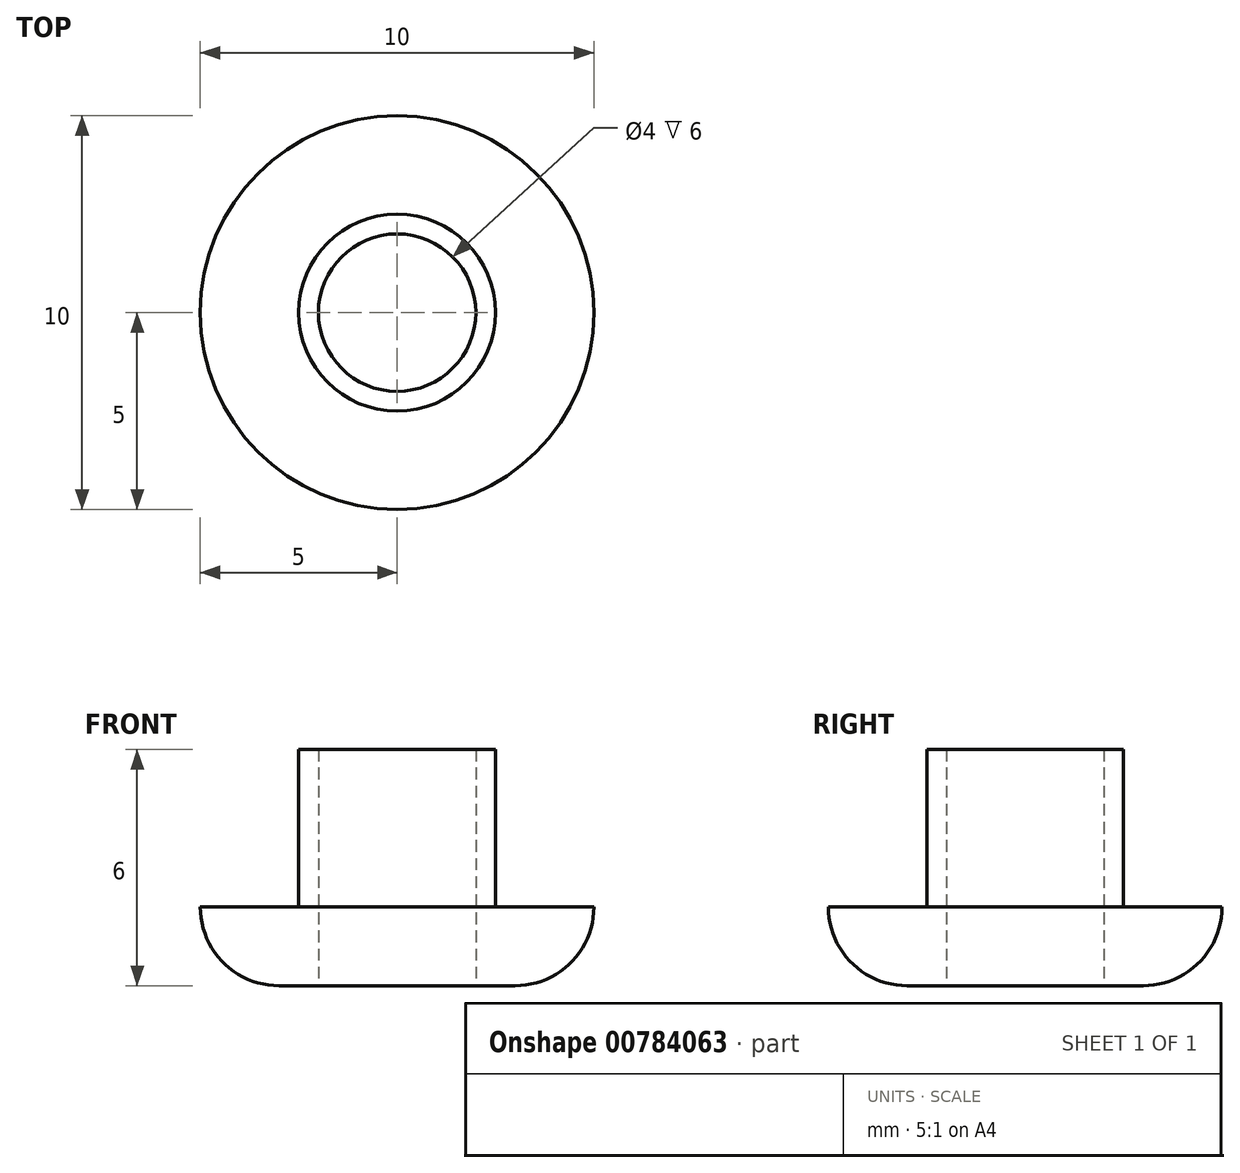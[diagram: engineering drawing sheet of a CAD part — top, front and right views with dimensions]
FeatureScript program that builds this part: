
annotation { "Feature Type Name" : "Feature", "Feature Type Description" : "" }
export const myFeature = defineFeature(function(context is Context, id is Id, definition is map)
    precondition{}
    {
        {
            var Q0;
            Q0=qCreatedBy(makeId("Top.planeOp"),FACE);
            var sketch = newSketch(context, id + "F0", { "sketchPlane" : qUnion([Q0])});
            skCircle(sketch, "E0", {"center": v(0, 0) * mm, "radius": 5 * mm});
            skCircle(sketch, "E1", {"center": v(0, 0) * mm, "radius": 2 * mm});
            skSolve(sketch);
        }
        {
            var Q0;
            Q0=makeQuery(id+"F0.imprint","IMPRINT",FACE,{"disambiguationData":[TD([[makeQuery(id+"F0.imprint","IMPRINT",EDGE,{"derivedFrom":sQuery(id+"F0.wireOp",EDGE,"E0")}),1.0]])]});
            var sketch = newSketch(context, id + "F1", { "sketchPlane" : qUnion([Q0])});
            skSolve(sketch);
        }
        {
            var Q0;
            Q0 = qSketchRegion(id + "F1", true);
            var Q1;
            Q1=makeQuery(id+"F0.imprint","IMPRINT",FACE,{"disambiguationData":[TD([[makeQuery(id+"F0.imprint","IMPRINT",EDGE,{"derivedFrom":sQuery(id+"F0.wireOp",EDGE,"E0")}),1.0]])]});
            extrude(context, id + "F2", {"entities" : qUnion([Q0, Q1]), "depth" : 2 * mm, "offsetDistance" : 25 * mm});
        }
        {
            var Q0;
            Q0=makeQuery(id+"F2.opExtrude","CAP_FACE",FACE,{"disambiguationData":[OSD([sQuery(id+"F0.wireOp",EDGE,"E0"),sQuery(id+"F0.wireOp",EDGE,"E1")])],"isStart":false});
            var sketch = newSketch(context, id + "F3", { "sketchPlane" : qUnion([Q0])});
            skCircle(sketch, "E2", {"center": v(0, 0) * mm, "radius": 2 * mm});
            skCircle(sketch, "E3", {"center": v(0, 0) * mm, "radius": 2.5 * mm});
            skSolve(sketch);
        }
        {
            var Q0;
            Q0=makeQuery(id+"F3.imprint","IMPRINT",FACE,{"disambiguationData":[TD([[makeQuery(id+"F3.imprint","IMPRINT",EDGE,{"derivedFrom":sQuery(id+"F3.wireOp",EDGE,"E2")}),-1.0]])]});
            extrude(context, id + "F4", {"entities" : qUnion([Q0]), "operationType" : NewBodyOperationType.ADD, "depth" : 4 * mm, "offsetDistance" : 25 * mm});
        }
        {
            var Q0;
            Q0=makeQuery(id+"F2.opExtrude","CAP_EDGE",EDGE,{"disambiguationData":[OSD([sQuery(id+"F0.wireOp",EDGE,"E0")])],"isStart":true});
            fillet(context, id + "F5", {"entities" : qUnion([Q0]), "radius" : 2 * mm, "tangentPropagation" : true, "allowEdgeOverflow" : false});
        }
    });
